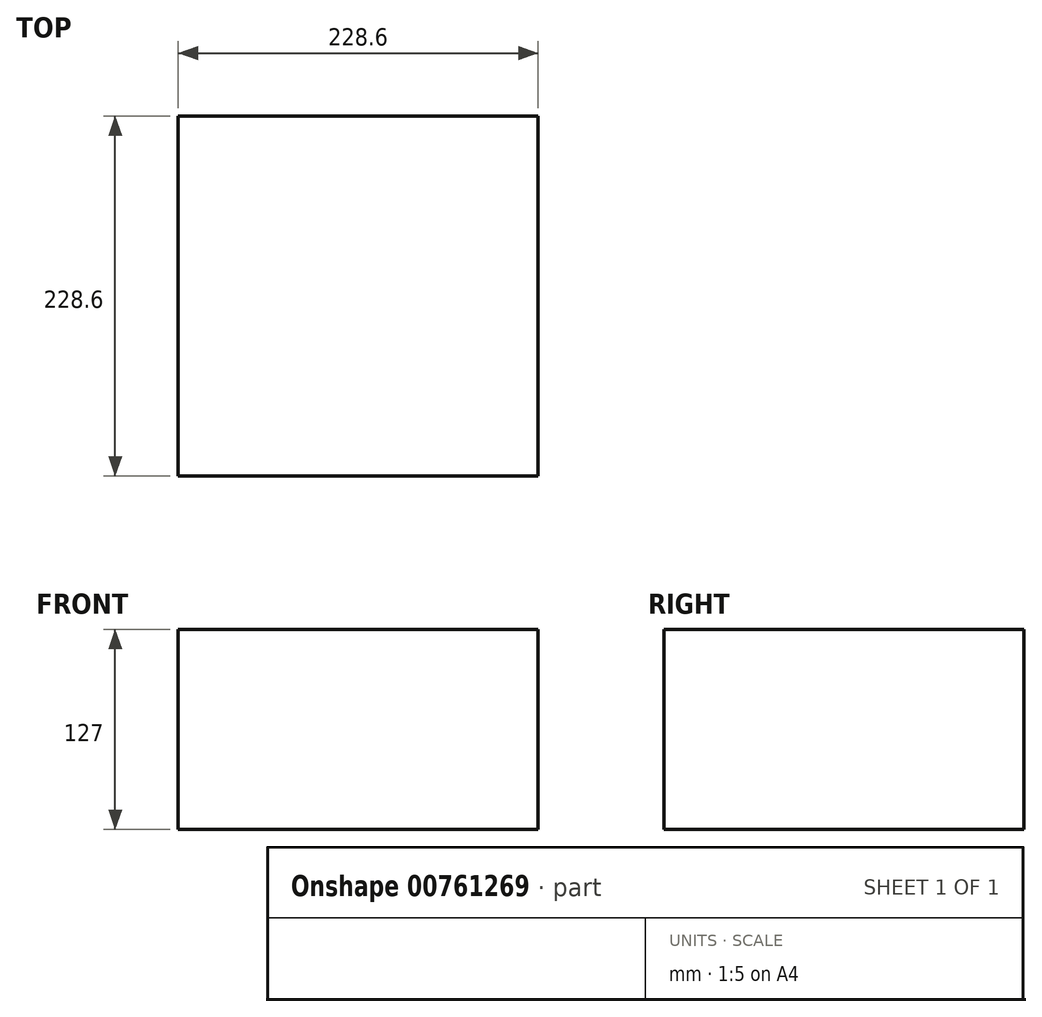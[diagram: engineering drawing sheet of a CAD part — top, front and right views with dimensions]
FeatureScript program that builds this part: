
annotation { "Feature Type Name" : "Feature", "Feature Type Description" : "" }
export const myFeature = defineFeature(function(context is Context, id is Id, definition is map)
    precondition{}
    {
        {
            var Q0;
            Q0=qCreatedBy(makeId("Top.planeOp"),FACE);
            var sketch = newSketch(context, id + "F0", { "sketchPlane" : qUnion([Q0])});
            skLineSegment(sketch, "E0.bottom", {"start": v(-114.3, 114.3) * mm, "end": v(114.3, 114.3) * mm});
            skLineSegment(sketch, "E0.top", {"start": v(-114.3, -114.3) * mm, "end": v(114.3, -114.3) * mm});
            skLineSegment(sketch, "E0.left", {"start": v(-114.3, 114.3) * mm, "end": v(-114.3, -114.3) * mm});
            skLineSegment(sketch, "E0.right", {"start": v(114.3, 114.3) * mm, "end": v(114.3, -114.3) * mm});
            skPoint(sketch, "E1", {"position": v(-114.3, 0) * mm});
            skPoint(sketch, "E2", {"position": v(0, 114.3) * mm});
            skSolve(sketch);
        }
        {
            var Q0;
            Q0 = qSketchRegion(id + "F0", true);
            extrude(context, id + "F1", {"entities" : qUnion([Q0]), "oppositeDirection" : true, "depth" : 127 * mm, "offsetDistance" : 25 * mm});
        }
    });
